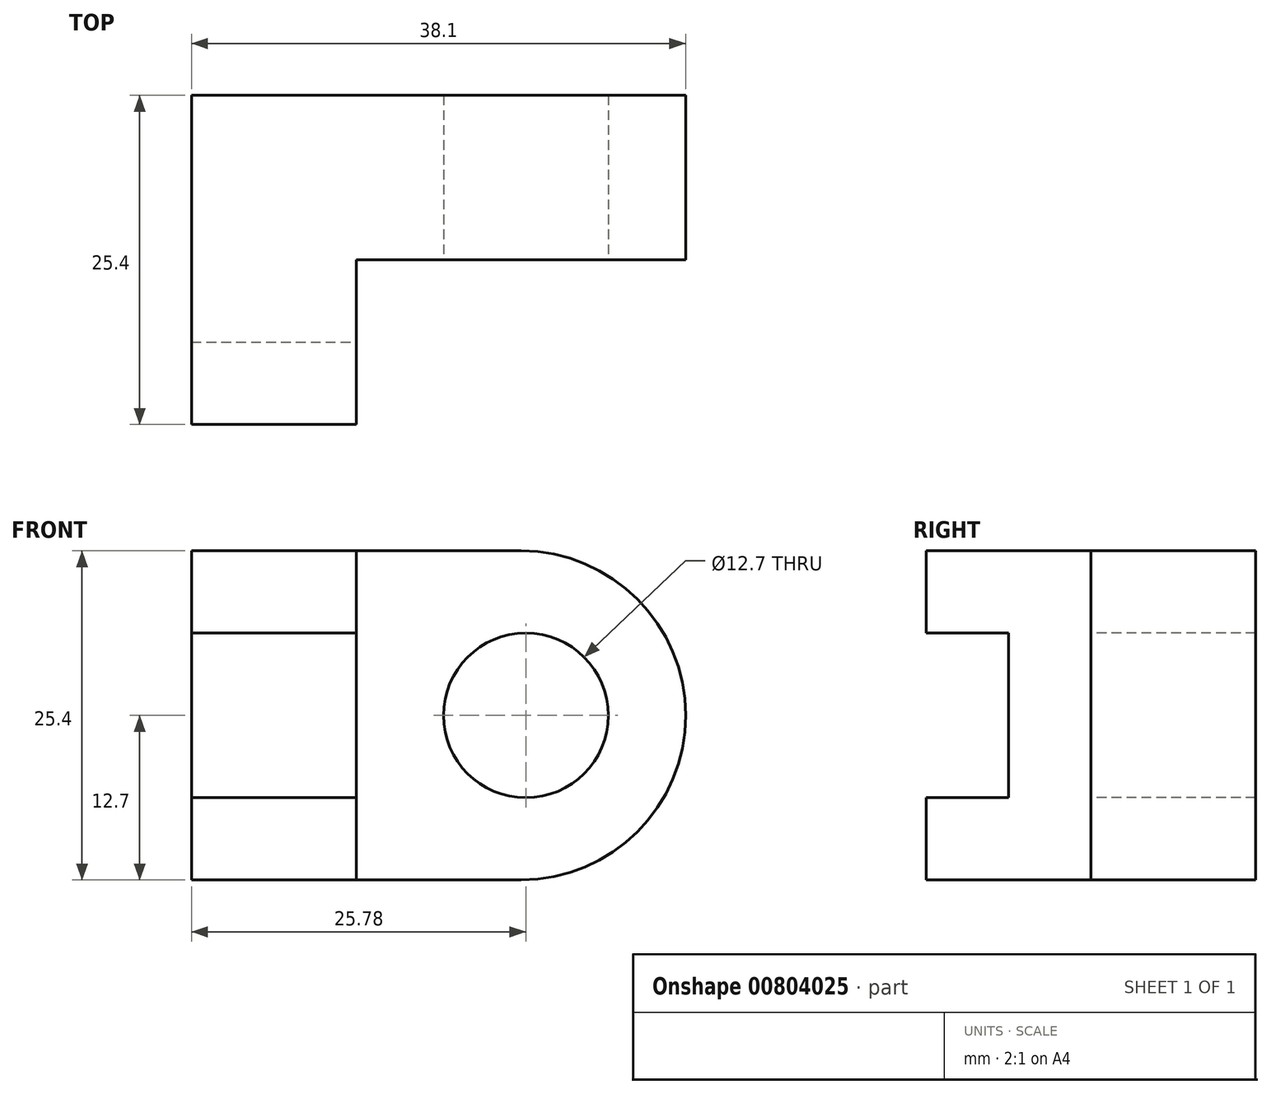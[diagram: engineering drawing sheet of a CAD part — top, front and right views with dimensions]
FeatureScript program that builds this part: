
annotation { "Feature Type Name" : "Feature", "Feature Type Description" : "" }
export const myFeature = defineFeature(function(context is Context, id is Id, definition is map)
    precondition{}
    {
        {
            var Q0;
            Q0=qCreatedBy(makeId("Front.planeOp"),FACE);
            var sketch = newSketch(context, id + "F0", { "sketchPlane" : qUnion([Q0])});
            skLineSegment(sketch, "E0", {"start": v(0, 0) * mm, "end": v(12.7, 0) * mm});
            skLineSegment(sketch, "E1", {"start": v(12.7, 0) * mm, "end": v(12.7, 25.4) * mm});
            skLineSegment(sketch, "E2", {"start": v(0, 25.4) * mm, "end": v(0, 0) * mm});
            skLineSegment(sketch, "E3", {"start": v(0, 25.4) * mm, "end": v(12.7, 25.4) * mm});
            skSolve(sketch);
        }
        {
            var Q0;
            Q0 = qSketchRegion(id + "F0", true);
            extrude(context, id + "F1", {"entities" : qUnion([Q0]), "depth" : 25.4 * mm, "offsetDistance" : 25.4 * mm});
        }
        {
            var Q0;
            Q0=makeQuery(id+"F1.opExtrude","SWEPT_FACE",FACE,{"disambiguationData":[OSD([sQuery(id+"F0.wireOp",EDGE,"E1")])]});
            var sketch = newSketch(context, id + "F2", { "sketchPlane" : qUnion([Q0])});
            skLineSegment(sketch, "E4", {"start": v(-12.7, 25.4) * mm, "end": v(-12.7, 0) * mm});
            skSolve(sketch);
        }
        {
            var Q0;
            {var subQ0=sQuery(id+"F2.wireOp",EDGE,"E4");Q0=makeQuery(id+"F2.imprint","IMPRINT",FACE,{"disambiguationData":[TD([[makeQuery(id+"F2.imprint","IMPRINT",EDGE,{"derivedFrom":subQ0}),1.0]])]});}
            extrude(context, id + "F3", {"entities" : qUnion([Q0]), "operationType" : NewBodyOperationType.ADD, "depth" : 25.4 * mm, "offsetDistance" : 25.4 * mm});
        }
        {
            var Q0;
            Q0=makeQuery(id+"F3.opExtrude","SWEPT_FACE",FACE,{"disambiguationData":[OSD([sQuery(id+"F2.wireOp",EDGE,"E4")])]});
            var sketch = newSketch(context, id + "F4", { "sketchPlane" : qUnion([Q0])});
            skArc(sketch, "E5", {"start": v(25.4, 0) * mm, "mid": v(38.1, 12.7) * mm, "end": v(25.4, 25.4) * mm});
            skSolve(sketch);
        }
        {
            var Q0;
            {var subQ0=sQuery(id+"F4.wireOp",EDGE,"E5");var subQ1=sQuery(id+"F2.wireOp",EDGE,"E4");var subQ4=makeQuery(id+"F3.opExtrude","CAP_EDGE",EDGE,{"disambiguationData":[OSD([subQ1])],"isStart":false});var subQ5=makeQuery(id+"F4.imprint","INTERSECT",VERTEX,{"derivedFrom":[subQ4,subQ0]});Q0=makeQuery(id+"F4.imprint","IMPRINT",FACE,{"disambiguationData":[TD([[makeQuery(id+"F4.imprint","IMPRINT",EDGE,{"disambiguationData":[TD([[subQ5,-1.0]])],"derivedFrom":subQ0}),-1.0]])]});}
            var Q1;
            {var subQ0=sQuery(id+"F4.wireOp",EDGE,"E5");var subQ1=sQuery(id+"F2.wireOp",EDGE,"E4");var subQ4=makeQuery(id+"F3.opExtrude","CAP_EDGE",EDGE,{"disambiguationData":[OSD([subQ1])],"isStart":false});var subQ5=makeQuery(id+"F4.imprint","INTERSECT",VERTEX,{"derivedFrom":[subQ4,subQ0]});Q1=makeQuery(id+"F4.imprint","IMPRINT",FACE,{"disambiguationData":[TD([[makeQuery(id+"F4.imprint","IMPRINT",EDGE,{"disambiguationData":[TD([[subQ5,1.0]])],"derivedFrom":subQ0}),-1.0]])]});}
            extrude(context, id + "F5", {"entities" : qUnion([Q0, Q1]), "operationType" : NewBodyOperationType.REMOVE, "oppositeDirection" : true, "depth" : 25.4 * mm, "offsetDistance" : 25.4 * mm});
        }
        {
            var Q0;
            Q0=makeQuery(id+"F1.opExtrude","SWEPT_FACE",FACE,{"disambiguationData":[OSD([sQuery(id+"F0.wireOp",EDGE,"E1")])]});
            var sketch = newSketch(context, id + "F6", { "sketchPlane" : qUnion([Q0])});
            skLineSegment(sketch, "E6", {"start": v(-25.4, 0) * mm, "end": v(-25.4, 6.35) * mm});
            skLineSegment(sketch, "E7", {"start": v(-25.4, 6.35) * mm, "end": v(-19.05, 6.35) * mm});
            skLineSegment(sketch, "E8", {"start": v(-19.05, 6.35) * mm, "end": v(-19.05, 19.05) * mm});
            skLineSegment(sketch, "E9", {"start": v(-19.05, 19.05) * mm, "end": v(-25.4, 19.05) * mm});
            skSolve(sketch);
        }
        {
            var Q0;
            {var subQ0=sQuery(id+"F6.wireOp",EDGE,"E7");Q0=makeQuery(id+"F6.imprint","IMPRINT",FACE,{"disambiguationData":[TD([[makeQuery(id+"F6.imprint","IMPRINT",EDGE,{"derivedFrom":subQ0}),1.0]])]});}
            extrude(context, id + "F7", {"entities" : qUnion([Q0]), "operationType" : NewBodyOperationType.REMOVE, "oppositeDirection" : true, "depth" : 25.4 * mm, "offsetDistance" : 25.4 * mm});
        }
        {
            var Q0;
            Q0=makeQuery(id+"F3.opExtrude","SWEPT_FACE",FACE,{"disambiguationData":[OSD([sQuery(id+"F2.wireOp",EDGE,"E4")])]});
            var sketch = newSketch(context, id + "F8", { "sketchPlane" : qUnion([Q0])});
            skLineSegment(sketch, "E10", {"start": v(13.08, 12.7) * mm, "end": v(19.43, 12.7) * mm, "construction": true});
            skPoint(sketch, "E10.startSnap0", {"position": v(12.7, 12.7) * mm});
            skLineSegment(sketch, "E11", {"start": v(19.43, 12.7) * mm, "end": v(32.13, 12.7) * mm, "construction": true});
            skCircle(sketch, "E12", {"center": v(25.78, 12.7) * mm, "radius": 6.35 * mm});
            skSolve(sketch);
        }
        {
            var Q0;
            Q0=makeQuery(id+"F8.imprint","IMPRINT",FACE,{"disambiguationData":[TD([[makeQuery(id+"F8.imprint","IMPRINT",EDGE,{"derivedFrom":sQuery(id+"F8.wireOp",EDGE,"E12")}),1.0]])]});
            extrude(context, id + "F9", {"entities" : qUnion([Q0]), "operationType" : NewBodyOperationType.REMOVE, "endBound" : BoundingType.THROUGH_ALL, "oppositeDirection" : true, "depth" : 25.4 * mm, "offsetDistance" : 25.4 * mm});
        }
    });
